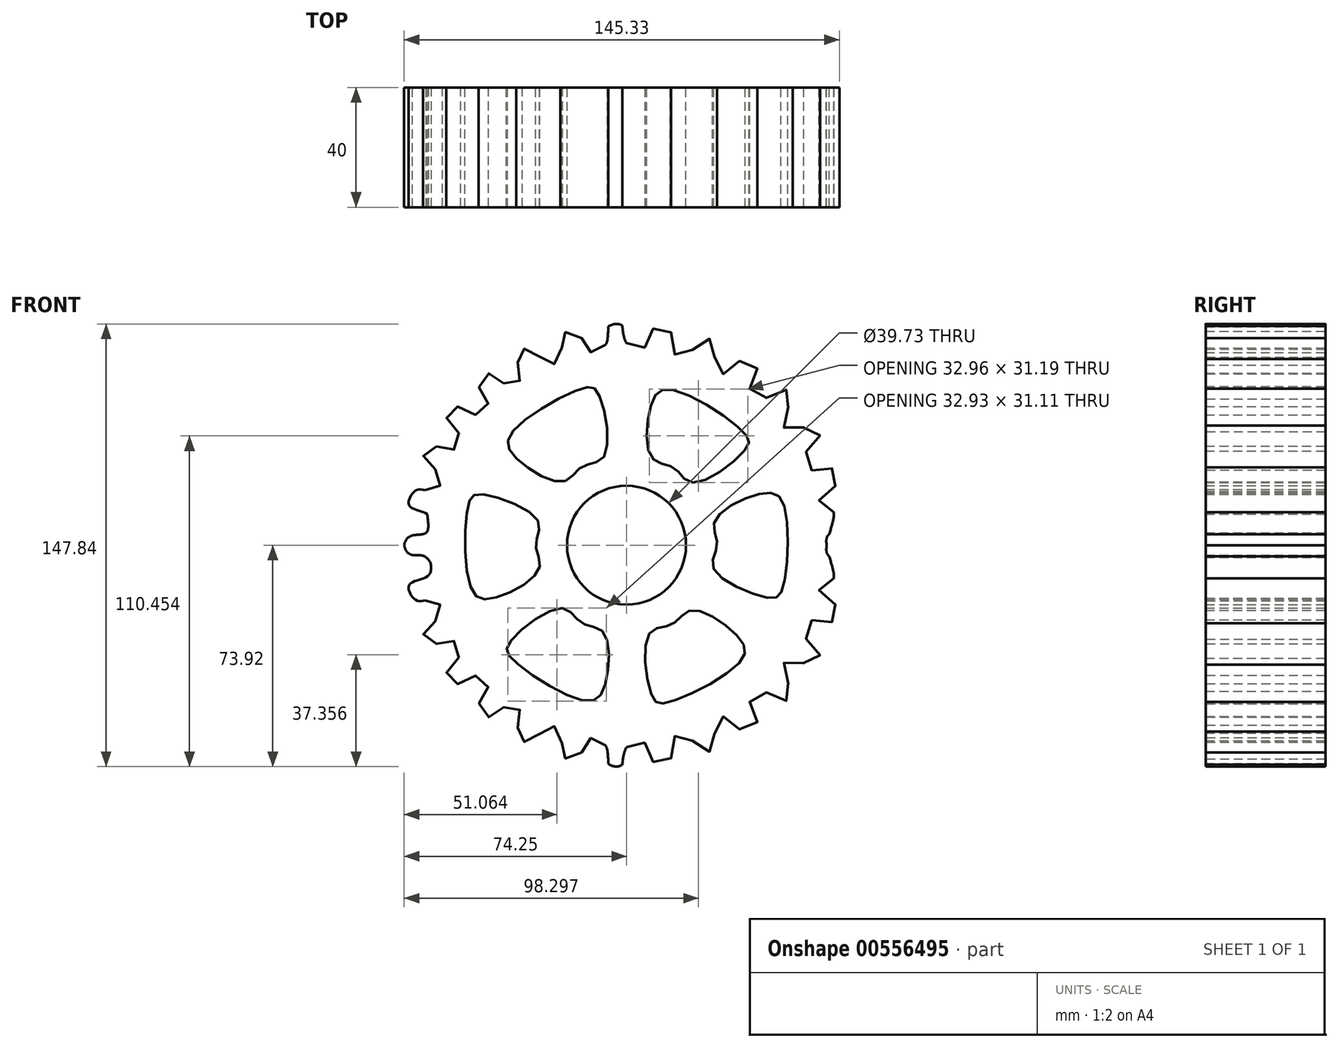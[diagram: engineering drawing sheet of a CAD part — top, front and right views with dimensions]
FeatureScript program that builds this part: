
annotation { "Feature Type Name" : "Feature", "Feature Type Description" : "" }
export const myFeature = defineFeature(function(context is Context, id is Id, definition is map)
    precondition{}
    {
        {
            var Q0;
            Q0=qCreatedBy(makeId("Front.planeOp"),FACE);
            var sketch = newSketch(context, id + "F0", { "sketchPlane" : qUnion([Q0])});
            skCircle(sketch, "E0", {"center": v(0, 0) * mm, "radius": 19.86 * mm});
            skLineSegment(sketch, "E1", {"start": v(-2.4, 0) * mm, "end": v(0, 0) * mm, "construction": true});
            skLineSegment(sketch, "E2", {"start": v(0, 0) * mm, "end": v(0, -67.5) * mm, "construction": true});
            skLineSegment(sketch, "E3", {"start": v(0, 0) * mm, "end": v(0, 61.43) * mm, "construction": true});
            skFitSpline(sketch, "E4", {"points": [v(29.13, -7.89) * mm, v(47.8, -17.62) * mm, v(52.1, -14.43) * mm, v(52.27, 14.3) * mm, v(44.77, 17.17) * mm, v(29.45, 8.07) * mm, v(30.24, 0) * mm, v(29.13, -7.89) * mm]});
            skFitSpline(sketch, "E5", {"points": [v(22.14, 20.94) * mm, v(39.9, 32.24) * mm, v(39.3, 37.57) * mm, v(14.5, 52.07) * mm, v(8.26, 47.01) * mm, v(8.48, 29.2) * mm, v(15.87, 25.85) * mm, v(22.14, 20.94) * mm]});
            skFitSpline(sketch, "E6", {"points": [v(-29.55, 8.19) * mm, v(-48.66, 17.04) * mm, v(-52.81, 13.65) * mm, v(-51.63, -15.05) * mm, v(-44, -17.57) * mm, v(-29.13, -7.77) * mm, v(-30.3, 0.26) * mm, v(-29.55, 8.19) * mm]});
            skFitSpline(sketch, "E7", {"points": [v(-7.5, 29.6) * mm, v(-9.34, 50.59) * mm, v(-14.35, 52.5) * mm, v(-38.66, 37.2) * mm, v(-37.04, 29.32) * mm, v(-21.14, 21.3) * mm, v(-14.76, 26.3) * mm, v(-7.5, 29.6) * mm]});
            skFitSpline(sketch, "E8", {"points": [v(-21.4, -21) * mm, v(-39.07, -32.48) * mm, v(-38.4, -37.8) * mm, v(-13.47, -52.07) * mm, v(-7.28, -46.95) * mm, v(-7.67, -29.14) * mm, v(-15.1, -25.86) * mm, v(-21.4, -21) * mm]});
            skFitSpline(sketch, "E9", {"points": [v(7.66, -29.45) * mm, v(8.56, -50.49) * mm, v(13.48, -52.62) * mm, v(38.44, -38.4) * mm, v(37.18, -30.47) * mm, v(21.64, -21.75) * mm, v(15.04, -26.47) * mm, v(7.66, -29.45) * mm]});
            skFitSpline(sketch, "E10", {"points": [v(-1.41, 73.36) * mm, v(1, 66.38) * mm, v(6.24, 66.11) * mm, v(8.65, 72.15) * mm, v(14.42, 72.29) * mm, v(14.96, 65.3) * mm, v(20.33, 63.03) * mm, v(24.35, 68.8) * mm, v(30.12, 67.05) * mm, v(28.92, 60.34) * mm, v(33.88, 57.25) * mm, v(38.71, 62.09) * mm, v(43.68, 58.87) * mm, v(41.13, 52.56) * mm, v(45.42, 48.8) * mm, v(51.87, 52.29) * mm, v(55.49, 48.67) * mm, v(51.6, 42.36) * mm, v(55.22, 37.8) * mm, v(61.4, 39.94) * mm, v(64.62, 35.65) * mm, v(59.38, 30.28) * mm, v(61.93, 25.04) * mm, v(67.84, 25.98) * mm, v(70.92, 21.02) * mm, v(64.88, 17.13) * mm, v(66.1, 11.49) * mm, v(72.4, 10.55) * mm, v(73.6, 5.18) * mm, v(66.9, 2.63) * mm, v(68.1, -12) * mm], "startDerivative": vector(28.3, -252) * mm, "endDerivative": vector(-212.04, -6.35) * mm});
            skFitSpline(sketch, "E11.MirrorCS", {"points": [v(-6.13, 72.96) * mm, v(-7.79, 65.76) * mm, v(-12.96, 64.94) * mm, v(-16, 70.69) * mm, v(-21.76, 70.2) * mm, v(-21.55, 63.2) * mm, v(-26.65, 60.37) * mm, v(-31.26, 65.68) * mm, v(-36.82, 63.33) * mm, v(-34.9, 56.78) * mm, v(-39.5, 53.19) * mm, v(-44.83, 57.48) * mm, v(-49.42, 53.75) * mm, v(-46.22, 47.74) * mm, v(-50.09, 43.55) * mm, v(-56.86, 46.34) * mm, v(-60.08, 42.35) * mm, v(-55.54, 36.49) * mm, v(-58.66, 31.57) * mm, v(-65.02, 33.04) * mm, v(-67.77, 28.43) * mm, v(-62, 23.65) * mm, v(-63.97, 18.17) * mm, v(-69.94, 18.48) * mm, v(-72.48, 13.21) * mm, v(-66.06, 9.99) * mm, v(-66.67, 4.25) * mm, v(-72.84, 2.65) * mm, v(-73.47, -2.82) * mm, v(-66.52, -4.64) * mm, v(-66.17, -19.31) * mm], "startDerivative": vector(-1.32, -253.58) * mm, "endDerivative": vector(211.51, 16.26) * mm});
            skFitSpline(sketch, "E12", {"points": [v(-6.91, 66.98) * mm, v(-6.13, 72.96) * mm, v(-1.41, 73.36) * mm, v(0, 67.5) * mm], "startDerivative": vector(-2.16, 20.52) * mm, "endDerivative": vector(0.05, -20.97) * mm});
            skFitSpline(sketch, "E13.MirrorCS", {"points": [v(-1.41, -73.36) * mm, v(1, -66.38) * mm, v(6.24, -66.11) * mm, v(8.65, -72.15) * mm, v(14.42, -72.29) * mm, v(14.96, -65.3) * mm, v(20.33, -63.03) * mm, v(24.35, -68.8) * mm, v(30.12, -67.05) * mm, v(28.92, -60.34) * mm, v(33.88, -57.25) * mm, v(38.71, -62.09) * mm, v(43.68, -58.87) * mm, v(41.13, -52.56) * mm, v(45.42, -48.8) * mm, v(51.87, -52.29) * mm, v(55.49, -48.67) * mm, v(51.6, -42.36) * mm, v(55.22, -37.8) * mm, v(61.4, -39.94) * mm, v(64.62, -35.65) * mm, v(59.38, -30.28) * mm, v(61.93, -25.04) * mm, v(67.84, -25.98) * mm, v(70.92, -21.02) * mm, v(64.88, -17.13) * mm, v(66.1, -11.49) * mm, v(72.4, -10.55) * mm, v(73.6, -5.18) * mm, v(66.9, -2.63) * mm, v(68.1, 12) * mm], "startDerivative": vector(28.3, 252) * mm, "endDerivative": vector(-212.04, 6.35) * mm});
            skLineSegment(sketch, "E14.MirrorCS", {"start": v(0, 0) * mm, "end": v(0, 67.5) * mm, "construction": true});
            skFitSpline(sketch, "E15.MirrorCS", {"points": [v(-6.13, -72.96) * mm, v(-7.79, -65.76) * mm, v(-12.96, -64.94) * mm, v(-16, -70.69) * mm, v(-21.76, -70.2) * mm, v(-21.55, -63.2) * mm, v(-26.65, -60.37) * mm, v(-31.26, -65.68) * mm, v(-36.82, -63.33) * mm, v(-34.9, -56.78) * mm, v(-39.5, -53.19) * mm, v(-44.83, -57.48) * mm, v(-49.42, -53.75) * mm, v(-46.22, -47.74) * mm, v(-50.09, -43.55) * mm, v(-56.86, -46.34) * mm, v(-60.08, -42.35) * mm, v(-55.54, -36.49) * mm, v(-58.66, -31.57) * mm, v(-65.02, -33.04) * mm, v(-67.77, -28.43) * mm, v(-62, -23.65) * mm, v(-63.97, -18.17) * mm, v(-69.94, -18.48) * mm, v(-72.48, -13.21) * mm, v(-66.06, -9.99) * mm, v(-66.67, -4.25) * mm, v(-72.84, -2.65) * mm, v(-73.47, 2.82) * mm, v(-66.52, 4.64) * mm, v(-66.17, 19.31) * mm], "startDerivative": vector(-1.32, 253.58) * mm, "endDerivative": vector(211.51, -16.26) * mm});
            skFitSpline(sketch, "E16", {"points": [v(-6.91, -66.98) * mm, v(-6.13, -72.96) * mm, v(-1.41, -73.36) * mm, v(0, -67.5) * mm], "startDerivative": vector(-2.16, -20.52) * mm, "endDerivative": vector(0.05, 20.97) * mm});
            skLineSegment(sketch, "E17", {"start": v(0, 0) * mm, "end": v(66.86, 0) * mm, "construction": true});
            skLineSegment(sketch, "E18", {"start": v(0, 0) * mm, "end": v(-74.25, 0) * mm, "construction": true});
            skSolve(sketch);
        }
        {
            var Q0;
            {var subQ0=sQuery(id+"F0.wireOp",EDGE,"E15.MirrorCS");var subQ1=sQuery(id+"F0.wireOp",EDGE,"E11.MirrorCS");var subQ2=makeQuery(id+"F0.imprint","INTERSECT",VERTEX,{"disambiguationData":[OD(0.0)],"derivedFrom":[subQ1,subQ0]});Q0=makeQuery(id+"F0.imprint","IMPRINT",FACE,{"disambiguationData":[TD([[makeQuery(id+"F0.imprint","IMPRINT",EDGE,{"disambiguationData":[TD([[subQ2,-1.0]])],"derivedFrom":subQ1}),1.0]])]});}
            var Q1;
            {var subQ0=sQuery(id+"F0.wireOp",EDGE,"E15.MirrorCS");var subQ1=sQuery(id+"F0.wireOp",EDGE,"E11.MirrorCS");var subQ2=makeQuery(id+"F0.imprint","INTERSECT",VERTEX,{"disambiguationData":[OD(2.0)],"derivedFrom":[subQ1,subQ0]});Q1=makeQuery(id+"F0.imprint","IMPRINT",FACE,{"disambiguationData":[TD([[makeQuery(id+"F0.imprint","IMPRINT",EDGE,{"disambiguationData":[TD([[subQ2,-1.0]])],"derivedFrom":subQ1}),-1.0]])]});}
            var Q2;
            {var subQ0=sQuery(id+"F0.wireOp",EDGE,"E15.MirrorCS");var subQ1=sQuery(id+"F0.wireOp",EDGE,"E11.MirrorCS");var subQ2=makeQuery(id+"F0.imprint","INTERSECT",VERTEX,{"disambiguationData":[OD(3.0)],"derivedFrom":[subQ1,subQ0]});Q2=makeQuery(id+"F0.imprint","IMPRINT",FACE,{"disambiguationData":[TD([[makeQuery(id+"F0.imprint","IMPRINT",EDGE,{"disambiguationData":[TD([[subQ2,-1.0]])],"derivedFrom":subQ1}),1.0]])]});}
            var Q3;
            {var subQ0=sQuery(id+"F0.wireOp",EDGE,"E15.MirrorCS");var subQ1=sQuery(id+"F0.wireOp",EDGE,"E11.MirrorCS");var subQ2=makeQuery(id+"F0.imprint","INTERSECT",VERTEX,{"disambiguationData":[OD(1.0)],"derivedFrom":[subQ1,subQ0]});Q3=makeQuery(id+"F0.imprint","IMPRINT",FACE,{"disambiguationData":[TD([[makeQuery(id+"F0.imprint","IMPRINT",EDGE,{"disambiguationData":[TD([[subQ2,1.0]])],"derivedFrom":subQ1}),-1.0]])]});}
            var Q4;
            Q4=makeQuery(id+"F0.imprint","IMPRINT",FACE,{"disambiguationData":[TD([[makeQuery(id+"F0.imprint","IMPRINT",EDGE,{"derivedFrom":sQuery(id+"F0.wireOp",EDGE,"E0")}),-1.0]])]});
            extrude(context, id + "F1", {"entities" : qUnion([Q0, Q1, Q2, Q3, Q4]), "depth" : 40 * mm, "offsetDistance" : 25 * mm});
        }
    });
